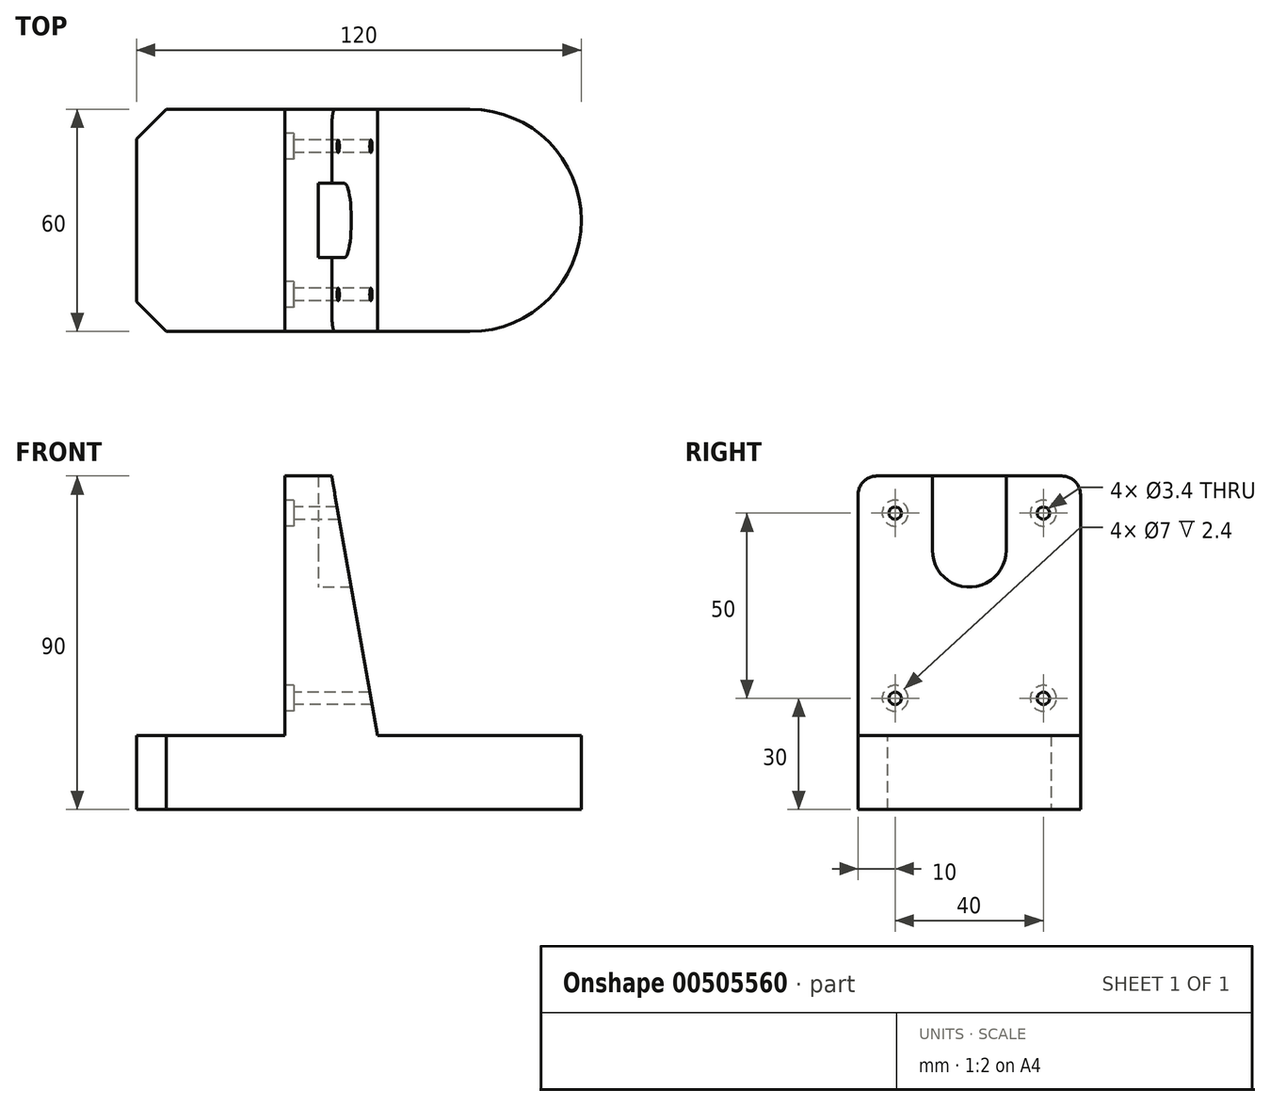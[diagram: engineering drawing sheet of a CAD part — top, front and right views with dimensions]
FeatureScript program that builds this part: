
annotation { "Feature Type Name" : "Feature", "Feature Type Description" : "" }
export const myFeature = defineFeature(function(context is Context, id is Id, definition is map)
    precondition{}
    {
        {
            var Q0;
            Q0=qCreatedBy(makeId("Top.planeOp"),FACE);
            var sketch = newSketch(context, id + "F0", { "sketchPlane" : qUnion([Q0])});
            skLineSegment(sketch, "E0.bottom", {"start": v(0, 0) * mm, "end": v(90, 0) * mm});
            skLineSegment(sketch, "E0.top", {"start": v(0, 60) * mm, "end": v(90, 60) * mm});
            skLineSegment(sketch, "E0.left", {"start": v(0, 0) * mm, "end": v(0, 60) * mm});
            skLineSegment(sketch, "E0.right", {"start": v(90, 0) * mm, "end": v(90, 60) * mm});
            skArc(sketch, "E1", {"start": v(90, 0) * mm, "mid": v(120, 30) * mm, "end": v(90, 60) * mm});
            skSolve(sketch);
        }
        {
            var Q0;
            Q0 = qSketchRegion(id + "F0", true);
            extrude(context, id + "F1", {"entities" : qUnion([Q0]), "depth" : 20 * mm});
        }
        {
            var Q0;
            Q0=makeQuery(id+"F1.opExtrude","SWEPT_EDGE",EDGE,{"disambiguationData":[OSD([sQuery(id+"F0.wireOp",EDGE,"E0.bottom"),sQuery(id+"F0.wireOp",EDGE,"E0.left")])]});
            var Q1;
            Q1=makeQuery(id+"F1.opExtrude","SWEPT_EDGE",EDGE,{"disambiguationData":[OSD([sQuery(id+"F0.wireOp",EDGE,"E0.top"),sQuery(id+"F0.wireOp",EDGE,"E0.left")])]});
            chamfer(context, id + "F2", {"entities" : qUnion([Q0, Q1]), "width" : 8 * mm, "tangentPropagation" : true});
        }
        {
            var Q0;
            Q0=qCreatedBy(makeId("Front.planeOp"),FACE);
            var sketch = newSketch(context, id + "F3", { "sketchPlane" : qUnion([Q0])});
            skLineSegment(sketch, "E2", {"start": v(40, 20) * mm, "end": v(65, 20) * mm});
            skLineSegment(sketch, "E3", {"start": v(65, 20) * mm, "end": v(52.66, 90) * mm});
            skLineSegment(sketch, "E4", {"start": v(52.66, 90) * mm, "end": v(40, 90) * mm});
            skLineSegment(sketch, "E5", {"start": v(40, 90) * mm, "end": v(40, 20) * mm});
            skSolve(sketch);
        }
        {
            var Q0;
            Q0 = qSketchRegion(id + "F3", true);
            var Q1;
            Q1=makeQuery(id+"F1.opExtrude","SWEPT_FACE",FACE,{"disambiguationData":[OSD([sQuery(id+"F0.wireOp",EDGE,"E0.top")])]});
            extrude(context, id + "F4", {"entities" : qUnion([Q0]), "operationType" : NewBodyOperationType.ADD, "endBound" : BoundingType.UP_TO_SURFACE, "oppositeDirection" : true, "endBoundEntityFace" : qUnion([Q1]), "depth" : 25 * mm});
        }
        {
            var Q0;
            Q0=makeQuery(id+"F4.opExtrude","CAP_EDGE",EDGE,{"disambiguationData":[OSD([sQuery(id+"F3.wireOp",EDGE,"E4")])],"isStart":true});
            var Q1;
            Q1=makeQuery(id+"F4.opExtrude","CAP_EDGE",EDGE,{"disambiguationData":[OSD([sQuery(id+"F3.wireOp",EDGE,"E4")])],"isStart":false});
            fillet(context, id + "F5", {"entities" : qUnion([Q0, Q1]), "radius" : 5 * mm, "tangentPropagation" : true, "allowEdgeOverflow" : false});
        }
        {
            var Q0;
            Q0=makeQuery(id+"F4.opExtrude","SWEPT_FACE",FACE,{"disambiguationData":[OSD([sQuery(id+"F3.wireOp",EDGE,"E5")])]});
            var sketch = newSketch(context, id + "F6", { "sketchPlane" : qUnion([Q0])});
            skLineSegment(sketch, "E6.bottom", {"start": v(-50, 30) * mm, "end": v(-10, 30) * mm, "construction": true});
            skLineSegment(sketch, "E6.top", {"start": v(-50, 80) * mm, "end": v(-10, 80) * mm, "construction": true});
            skLineSegment(sketch, "E6.left", {"start": v(-50, 30) * mm, "end": v(-50, 80) * mm, "construction": true});
            skLineSegment(sketch, "E6.right", {"start": v(-10, 30) * mm, "end": v(-10, 80) * mm, "construction": true});
            skPoint(sketch, "E7", {"position": v(-30, 80) * mm});
            skPoint(sketch, "E8", {"position": v(-30, 90) * mm});
            skSolve(sketch);
        }
        {
            var Q0;
            Q0=sQuery(id+"F6.wireOp",VERTEX,"E6.left.end");
            var Q1;
            Q1=sQuery(id+"F6.wireOp",VERTEX,"E6.left.start");
            var Q2;
            Q2=sQuery(id+"F6.wireOp",VERTEX,"E6.right.start");
            var Q3;
            Q3=sQuery(id+"F6.wireOp",VERTEX,"E6.right.end");
            var Q4;
            Q4=makeQuery(id+"F1.opExtrude","SWEPT_BODY",BODY,{"disambiguationData":[OSD([sQuery(id+"F0.wireOp",EDGE,"E0.bottom"),sQuery(id+"F0.wireOp",EDGE,"E0.top"),sQuery(id+"F0.wireOp",EDGE,"E0.left"),sQuery(id+"F0.wireOp",EDGE,"E1")])]});
            hole(context, id + "F7", {"style" : HoleStyle.C_BORE, "endStyle" : HoleEndStyle.THROUGH, "holeDiameter" : 3.4 * mm, "cBoreDiameter" : 7 * mm, "cBoreDepth" : 2.4 * mm, "isTappedThrough" : true, "tappedDepth" : 37.5 * mm, "tapClearance" : 3, "startFromSketch" : true, "locations" : qUnion([Q0, Q1, Q2, Q3]), "scope" : qUnion([Q4])});
        }
        {
            var Q0;
            Q0=makeQuery(id+"F4.opExtrude","SWEPT_FACE",FACE,{"disambiguationData":[OSD([sQuery(id+"F3.wireOp",EDGE,"E5")])]});
            cPlane(context, id + "F8", {"entities" : qUnion([Q0]), "cplaneType" : CPlaneType.OFFSET, "offset" : 9 * mm, "oppositeDirection" : true, "width" : 150 * mm, "height" : 150 * mm});
        }
        {
            var Q0;
            Q0=qCreatedBy(id+"F8.planeOp",FACE);
            var sketch = newSketch(context, id + "F9", { "sketchPlane" : qUnion([Q0])});
            skLineSegment(sketch, "E9.bottom", {"start": v(-20, 90) * mm, "end": v(-40, 90) * mm});
            skLineSegment(sketch, "E9.top", {"start": v(-20, 70) * mm, "end": v(-40, 70) * mm});
            skLineSegment(sketch, "E9.left", {"start": v(-20, 90) * mm, "end": v(-20, 70) * mm});
            skLineSegment(sketch, "E9.right", {"start": v(-40, 90) * mm, "end": v(-40, 70) * mm});
            skPoint(sketch, "E10", {"position": v(-30, 90) * mm});
            skArc(sketch, "E11", {"start": v(-40, 70) * mm, "mid": v(-30, 60) * mm, "end": v(-20, 70) * mm});
            skSolve(sketch);
        }
        {
            var Q0;
            Q0 = qSketchRegion(id + "F9", true);
            extrude(context, id + "F10", {"entities" : qUnion([Q0]), "operationType" : NewBodyOperationType.REMOVE, "endBound" : BoundingType.UP_TO_NEXT, "oppositeDirection" : true, "depth" : 25 * mm});
        }
    });
